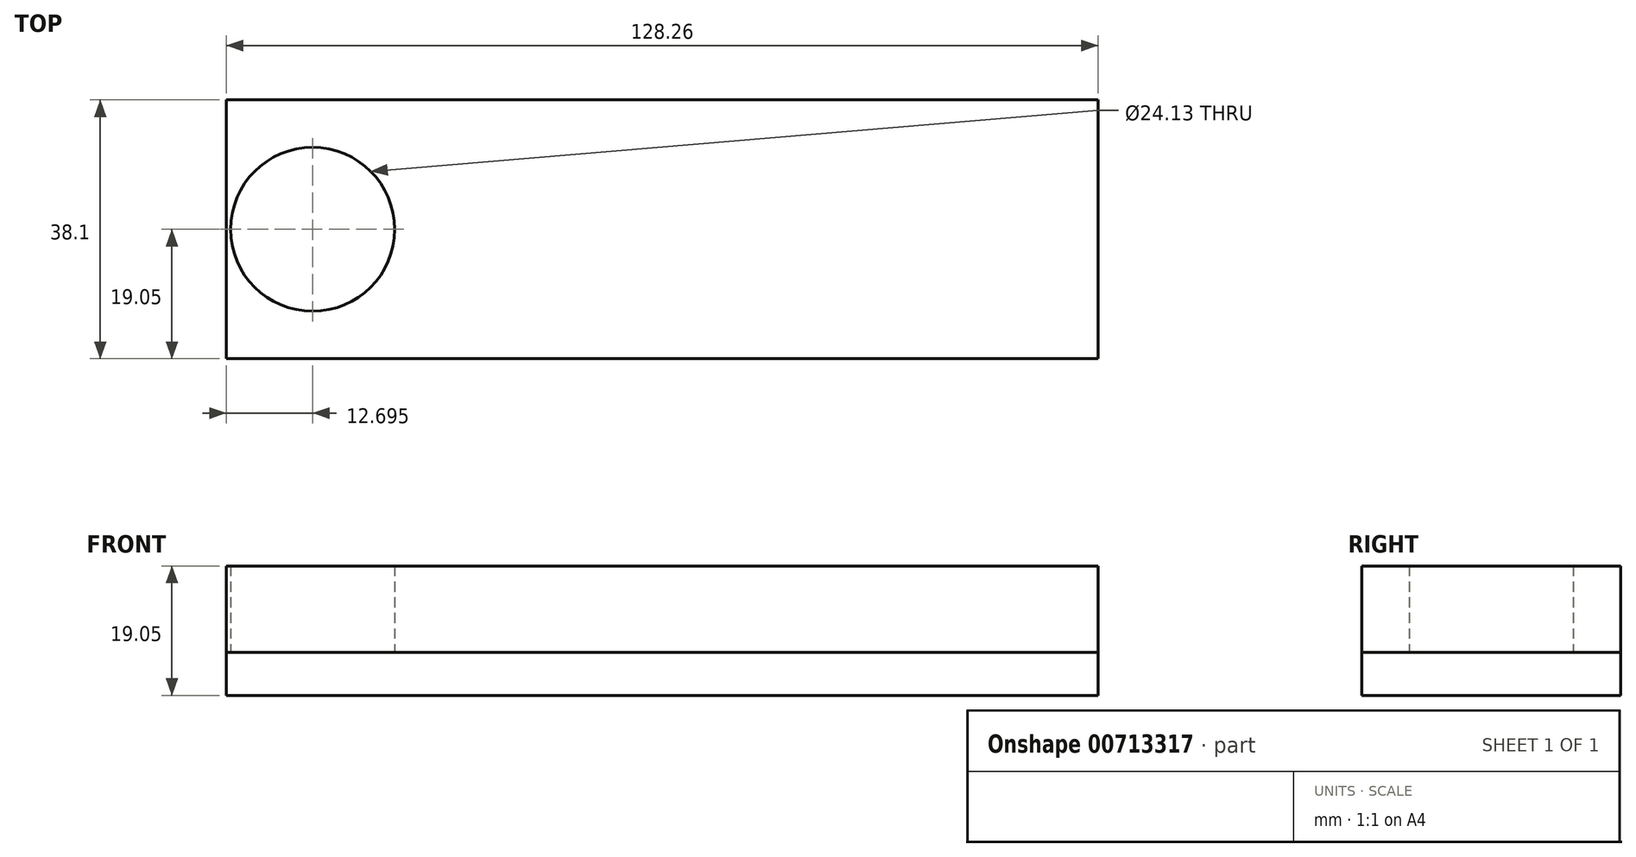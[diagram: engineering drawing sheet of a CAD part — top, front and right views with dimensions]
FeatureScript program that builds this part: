
annotation { "Feature Type Name" : "Feature", "Feature Type Description" : "" }
export const myFeature = defineFeature(function(context is Context, id is Id, definition is map)
    precondition{}
    {
        {
            var Q0;
            Q0=qCreatedBy(makeId("Top.planeOp"),FACE);
            var sketch = newSketch(context, id + "F0", { "sketchPlane" : qUnion([Q0])});
            skLineSegment(sketch, "E0.bottom", {"start": v(64.13, 19.05) * mm, "end": v(-64.13, 19.05) * mm});
            skLineSegment(sketch, "E0.top", {"start": v(64.13, -19.05) * mm, "end": v(-64.13, -19.05) * mm});
            skLineSegment(sketch, "E0.left", {"start": v(64.13, 19.05) * mm, "end": v(64.13, -19.05) * mm});
            skLineSegment(sketch, "E0.right", {"start": v(-64.13, 19.05) * mm, "end": v(-64.13, -19.05) * mm});
            skPoint(sketch, "E0.middle", {"position": v(0, 0) * mm});
            skLineSegment(sketch, "E1", {"start": v(0, -19.05) * mm, "end": v(0, 19.05) * mm, "construction": true});
            skSolve(sketch);
        }
        {
            var Q0;
            Q0=makeQuery(id+"F0.imprint","IMPRINT",FACE,{"disambiguationData":[TD([[makeQuery(id+"F0.imprint","IMPRINT",EDGE,{"derivedFrom":sQuery(id+"F0.wireOp",EDGE,"E0.bottom")}),1.0]])]});
            extrude(context, id + "F1", {"entities" : qUnion([Q0]), "depth" : 6.35 * mm, "offsetDistance" : 25.4 * mm});
        }
        {
            var Q0;
            Q0=makeQuery(id+"F1.opExtrude","CAP_FACE",FACE,{"disambiguationData":[OSD([sQuery(id+"F0.wireOp",EDGE,"E0.bottom"),sQuery(id+"F0.wireOp",EDGE,"E0.top"),sQuery(id+"F0.wireOp",EDGE,"E0.left"),sQuery(id+"F0.wireOp",EDGE,"E0.right")])],"isStart":false});
            var sketch = newSketch(context, id + "F2", { "sketchPlane" : qUnion([Q0])});
            skCircle(sketch, "E2", {"center": v(51.43, 0) * mm, "radius": 12.07 * mm});
            skLineSegment(sketch, "E3", {"start": v(0, -19.05) * mm, "end": v(0, 19.05) * mm, "construction": true});
            skCircle(sketch, "E4.MirrorC", {"center": v(-51.43, 0) * mm, "radius": 12.07 * mm});
            skSolve(sketch);
        }
        {
            var Q0;
            Q0=makeQuery(id+"F2.imprint","IMPRINT",FACE,{"disambiguationData":[TD([[makeQuery(id+"F2.imprint","IMPRINT",EDGE,{"derivedFrom":sQuery(id+"F2.wireOp",EDGE,"E4.MirrorC")}),-1.0]])]});
            var Q1;
            Q1=makeQuery(id+"F2.imprint","IMPRINT",FACE,{"disambiguationData":[TD([[makeQuery(id+"F2.imprint","IMPRINT",EDGE,{"derivedFrom":sQuery(id+"F2.wireOp",EDGE,"E2")}),1.0]])]});
            var Q2;
            Q2=sQuery(id+"F2.wireOp",EDGE,"E2");
            var Q3;
            Q3=sQuery(id+"F2.wireOp",EDGE,"E4.MirrorC");
            extrude(context, id + "F3", {"entities" : qUnion([Q0, Q1]), "surfaceEntities" : qUnion([Q2, Q3]), "depth" : 12.7 * mm, "offsetDistance" : 25.4 * mm});
        }
    });
